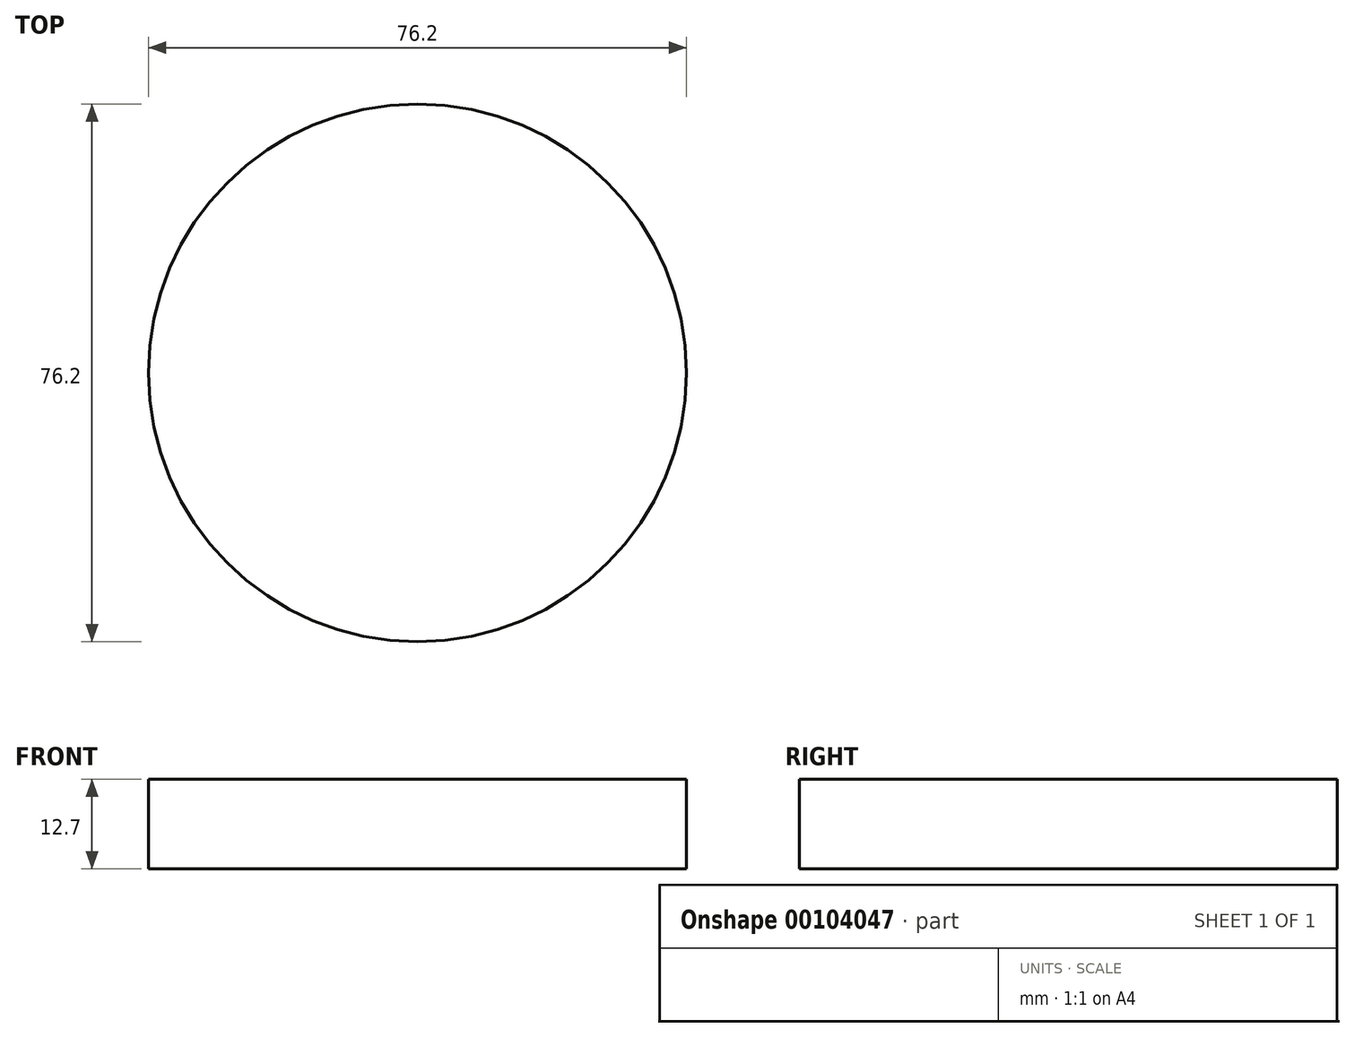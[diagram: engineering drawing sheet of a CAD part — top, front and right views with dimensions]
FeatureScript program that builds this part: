
annotation { "Feature Type Name" : "Feature", "Feature Type Description" : "" }
export const myFeature = defineFeature(function(context is Context, id is Id, definition is map)
    precondition{}
    {
        {
            var Q0;
            Q0=qCreatedBy(makeId("Top.planeOp"),FACE);
            var sketch = newSketch(context, id + "F0", { "sketchPlane" : qUnion([Q0])});
            skCircle(sketch, "E0", {"center": v(0, 0) * mm, "radius": 38.1 * mm});
            skSolve(sketch);
        }
        {
            var Q0;
            Q0 = qSketchRegion(id + "F0", true);
            extrude(context, id + "F1", {"entities" : qUnion([Q0]), "depth" : 12.7 * mm});
        }
        {
            var Q0;
            Q0=makeQuery(id+"F1.opExtrude","CAP_FACE",FACE,{"disambiguationData":[OSD([sQuery(id+"F0.wireOp",EDGE,"E0")])],"isStart":false});
            var sketch = newSketch(context, id + "F2", { "sketchPlane" : qUnion([Q0])});
            skCircle(sketch, "E1", {"center": v(0, 0) * mm, "radius": 31.75 * mm});
            skSolve(sketch);
        }
    });
